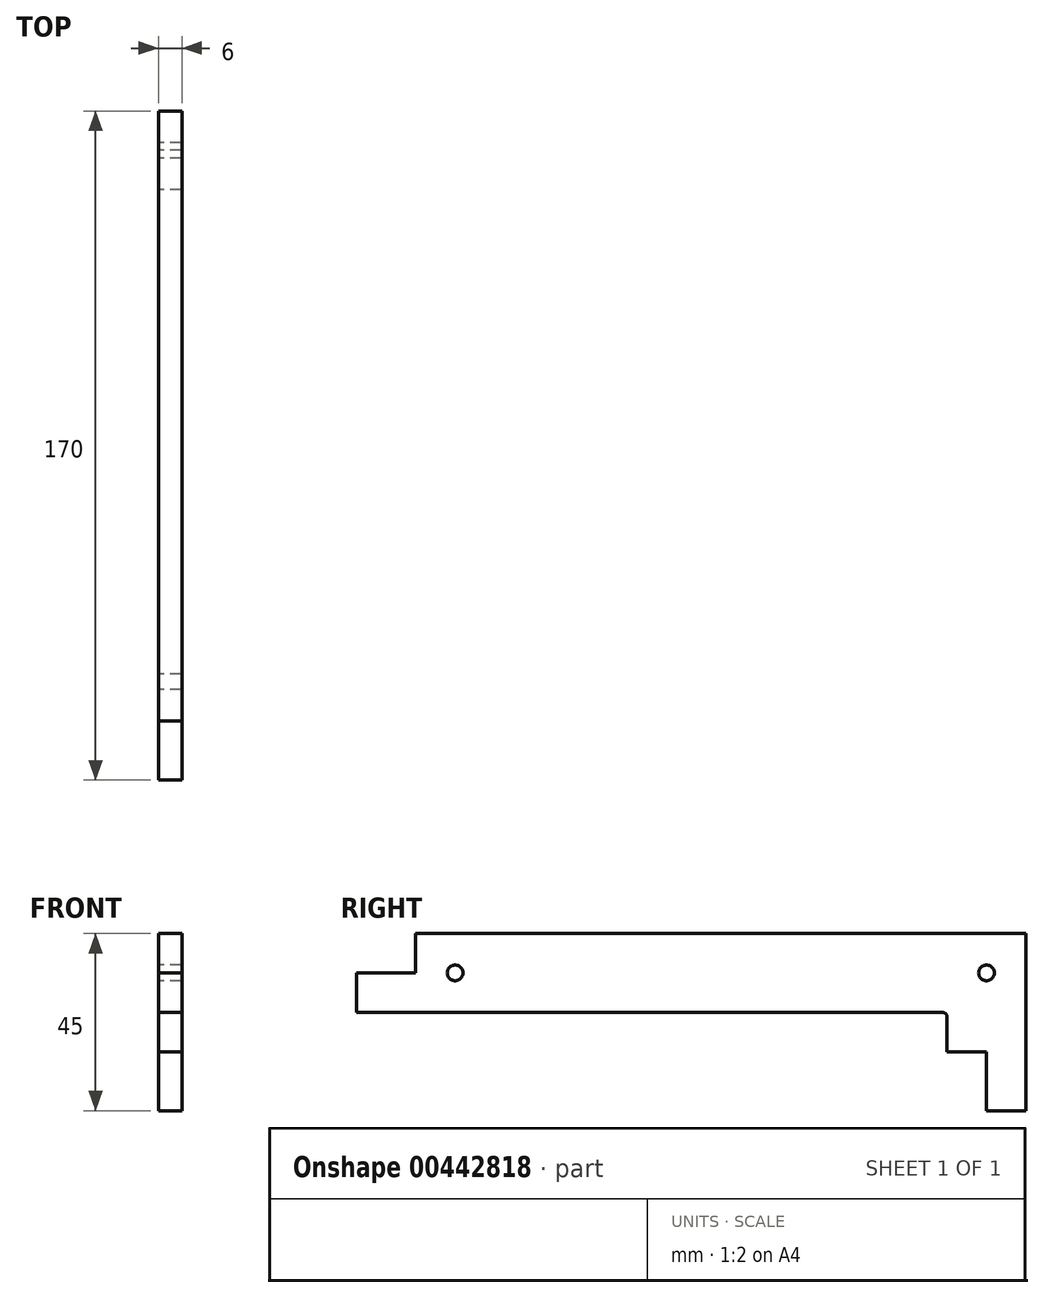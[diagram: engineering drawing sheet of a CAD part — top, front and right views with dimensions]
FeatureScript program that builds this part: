
annotation { "Feature Type Name" : "Feature", "Feature Type Description" : "" }
export const myFeature = defineFeature(function(context is Context, id is Id, definition is map)
    precondition{}
    {
        {
            var Q0;
            Q0=qCreatedBy(makeId("Right.planeOp"),FACE);
            var sketch = newSketch(context, id + "F0", { "sketchPlane" : qUnion([Q0])});
            skLineSegment(sketch, "E0.top", {"start": v(-1.27, 250) * mm, "end": v(-150, 250) * mm});
            skLineSegment(sketch, "E0.left", {"start": v(0, 240) * mm, "end": v(0, 248.73) * mm});
            skPoint(sketch, "E1.visualSharp", {"position": v(0, 250) * mm});
            skArc(sketch, "E1.filletArc", {"start": v(0, 248.73) * mm, "mid": v(-0.37, 249.63) * mm, "end": v(-1.27, 250) * mm});
            skPoint(sketch, "E2.visualSharp", {"position": v(0, 0) * mm});
            skLineSegment(sketch, "E3", {"start": v(-135, 270) * mm, "end": v(20, 270) * mm});
            skLineSegment(sketch, "E4", {"start": v(20, 270) * mm, "end": v(20, 225) * mm});
            skLineSegment(sketch, "E5", {"start": v(20, 225) * mm, "end": v(10, 225) * mm});
            skLineSegment(sketch, "E6", {"start": v(10, 225) * mm, "end": v(10, 240) * mm});
            skLineSegment(sketch, "E7", {"start": v(10, 240) * mm, "end": v(0, 240) * mm});
            skCircle(sketch, "E8", {"center": v(10, 260) * mm, "radius": 2 * mm});
            skLineSegment(sketch, "E9", {"start": v(-135, 270) * mm, "end": v(-135, 260) * mm});
            skLineSegment(sketch, "E10", {"start": v(-135, 260) * mm, "end": v(-150, 260) * mm});
            skLineSegment(sketch, "E11", {"start": v(-150, 260) * mm, "end": v(-150, 250) * mm});
            skCircle(sketch, "E12", {"center": v(-125, 260) * mm, "radius": 2 * mm});
            skSolve(sketch);
        }
        {
            var Q0;
            Q0=qSketchRegion(id+"F0",true);
            extrude(context, id + "F1", {"entities" : qUnion([Q0]), "depth" : 6 * mm, "offsetDistance" : 25 * mm});
        }
    });
